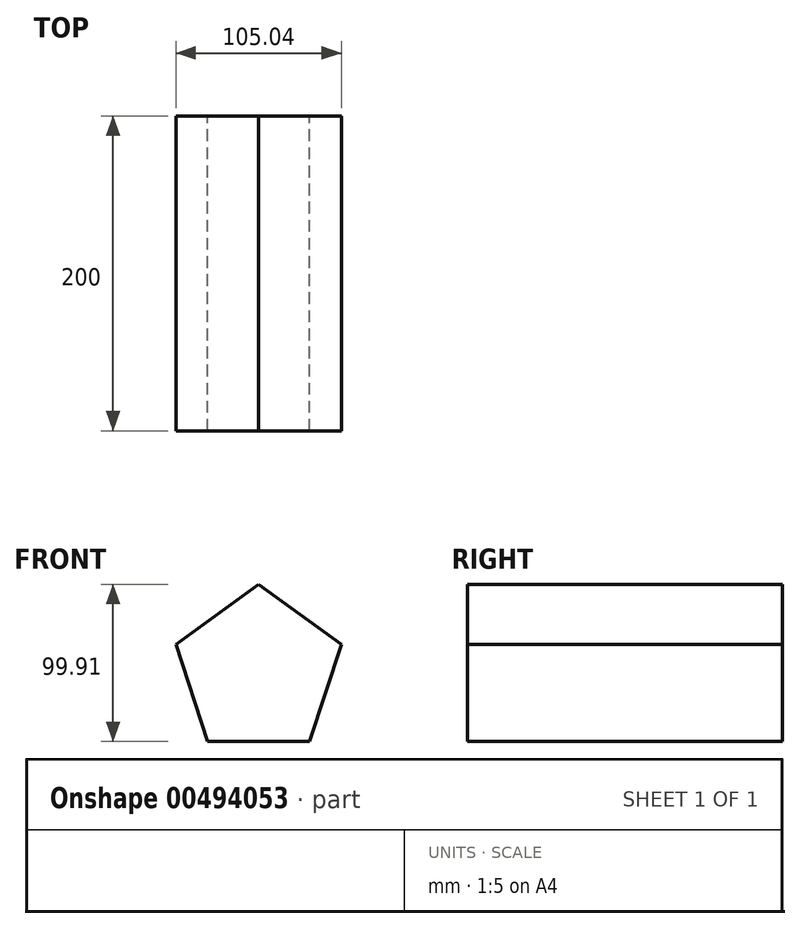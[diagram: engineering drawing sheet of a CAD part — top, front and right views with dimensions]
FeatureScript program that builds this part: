
annotation { "Feature Type Name" : "Feature", "Feature Type Description" : "" }
export const myFeature = defineFeature(function(context is Context, id is Id, definition is map)
    precondition{}
    {
        {
            var Q0;
            Q0=qCreatedBy(makeId("Front.planeOp"),FACE);
            var sketch = newSketch(context, id + "F0", { "sketchPlane" : qUnion([Q0])});
            skCircle(sketch, "E0.cCircle", {"center": v(0, 0) * mm, "radius": 55.23 * mm, "construction": true});
            skLineSegment(sketch, "E0.0", {"start": v(0, 55.23) * mm, "end": v(52.52, 17.07) * mm});
            skLineSegment(sketch, "E0.1", {"start": v(52.52, 17.07) * mm, "end": v(32.46, -44.68) * mm});
            skLineSegment(sketch, "E0.2", {"start": v(32.46, -44.68) * mm, "end": v(-32.46, -44.68) * mm});
            skLineSegment(sketch, "E0.3", {"start": v(-32.46, -44.68) * mm, "end": v(-52.52, 17.07) * mm});
            skLineSegment(sketch, "E0.4", {"start": v(-52.52, 17.07) * mm, "end": v(0, 55.23) * mm});
            skSolve(sketch);
        }
        {
            var Q0;
            Q0=makeQuery(id+"F0.imprint","IMPRINT",FACE,{"disambiguationData":[TD([[makeQuery(id+"F0.imprint","IMPRINT",EDGE,{"derivedFrom":sQuery(id+"F0.wireOp",EDGE,"E0.0")}),-1.0]])]});
            extrude(context, id + "F1", {"entities" : qUnion([Q0]), "depth" : 200 * mm});
        }
    });
